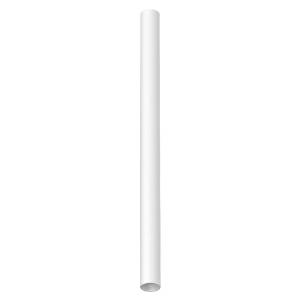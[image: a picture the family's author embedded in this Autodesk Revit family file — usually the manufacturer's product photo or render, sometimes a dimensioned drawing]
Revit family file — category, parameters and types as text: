
# Revit family: hangover_plug_decor_o30_l450__810-0393
name_source: partatom
category: Leuchten
revit_build: Autodesk Revit 2016 (Build: 20190508_0715(x64)
units: mm (PartAtom-declared; Revit-internal decimal feet)

## family parameters
Basisbauteil = Fläche
Beim Laden mit Abzugskörper schneiden = Nein
Bemaßung runder Anschluss = Durchmesser verwenden
Gemeinsam genutzt = Nein
Lichtquelle = Nein
Raumberechnungspunkt = Nein
Teiletyp = Normal

## types (1)
- 810-0393-
    Beschreibung = With 2 powder coated options 841 colour combinations can be achieved. The integrated ballast allows for an operation with.
    Height = 450 mm
    Hersteller = Prolicht
    Lampe = 0 x
    Length = 28 mm
    Luminous efficacy = 0 lm/W
    ModVariant = Nein
    Modell = 810-0393
    Number of Poles = 1
    OnlyDefault = Ja
    Power Factor = 1
    Product Name = HANGOVER PLUG DECOR Ø30 L450
    Product group = Luminaires
    ProductGroupID = 0
    Protection Class = Protection class
    Protection Degree = Degree of protection
    RLX_Detail_Level = 1
    RlxData = <blob elided: 40129 chars, md5=517f5e00>
    Scheinlast = 0 VA
    Standby Power = 0 W
    System Light Flux = 0 lm
    System Power = 0 W
    Typenbild = 810-0393.jpg
    URL = http://relux.com
    VarID = 810-0393-
    Voltage = 0 V
    Vorgabe-Ansicht = 1800 mm
    Weight = 0.00 kg
    Width = 0 mm  [stored 0 ft]

note: [stored X ft] marks values corroborated as IEEE doubles in the binary element streams (Revit-internal decimal feet)

## geometry (parser evidence)
native form markers: Sweep x8
no freeform markers — native parametric forms only
